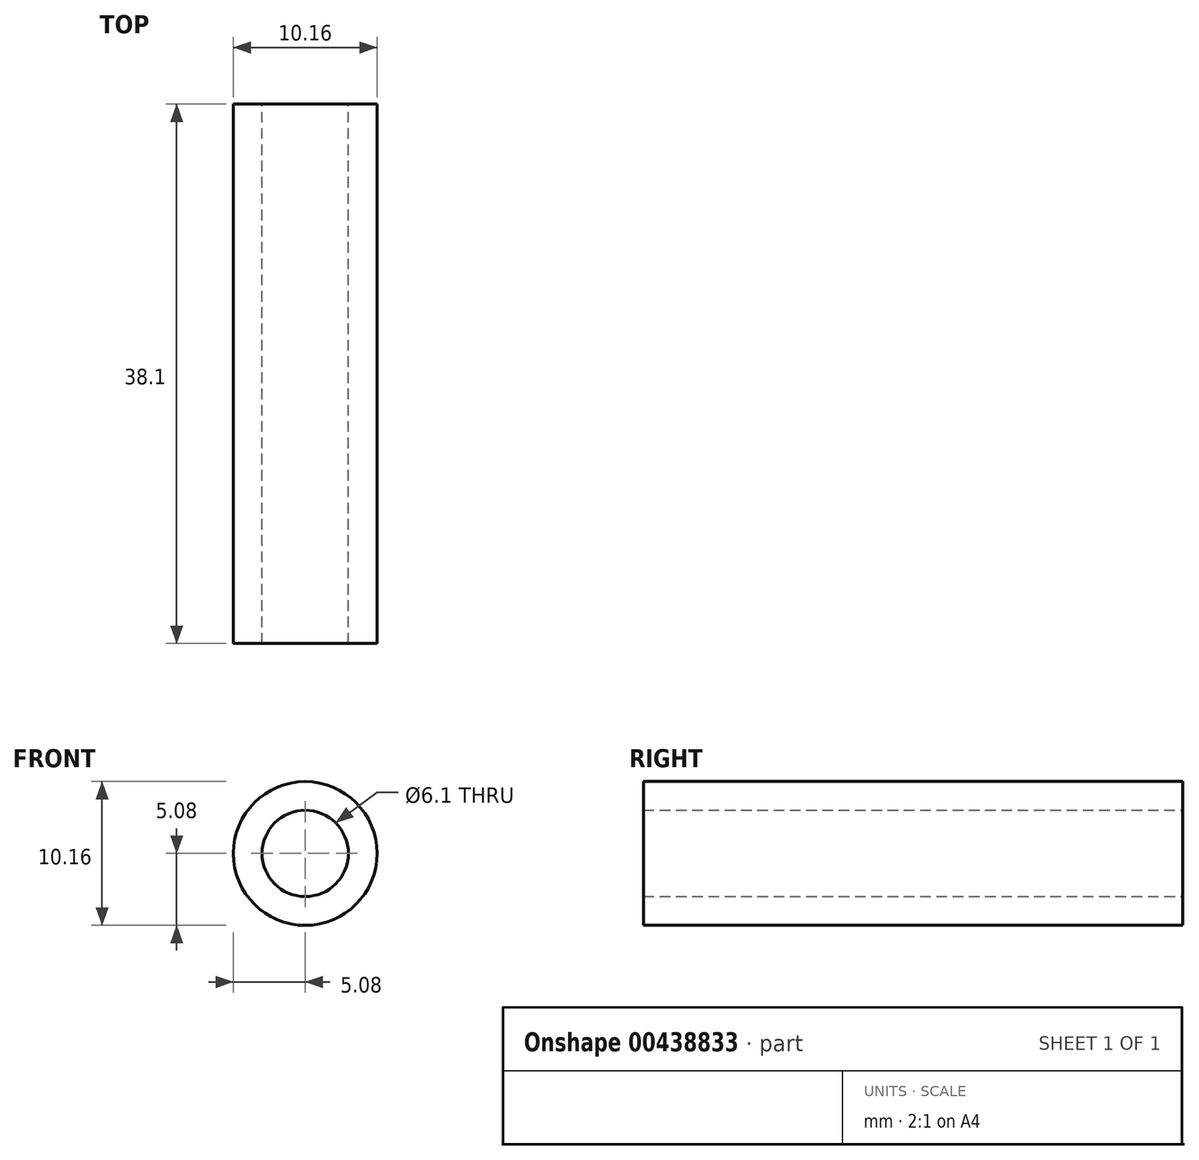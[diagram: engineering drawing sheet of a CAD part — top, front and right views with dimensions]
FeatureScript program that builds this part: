
annotation { "Feature Type Name" : "Feature", "Feature Type Description" : "" }
export const myFeature = defineFeature(function(context is Context, id is Id, definition is map)
    precondition{}
    {
        {
            var Q0;
            Q0=qCreatedBy(makeId("Front.planeOp"),FACE);
            var sketch = newSketch(context, id + "F0", { "sketchPlane" : qUnion([Q0])});
            skCircle(sketch, "E0", {"center": v(0, 0) * mm, "radius": 3.05 * mm});
            skCircle(sketch, "E1", {"center": v(0, 0) * mm, "radius": 5.08 * mm});
            skSolve(sketch);
        }
        {
            var Q0;
            Q0=makeQuery(id+"F0.imprint","IMPRINT",FACE,{"disambiguationData":[TD([[makeQuery(id+"F0.imprint","IMPRINT",EDGE,{"derivedFrom":sQuery(id+"F0.wireOp",EDGE,"E0")}),-1.0]])]});
            extrude(context, id + "F1", {"entities" : qUnion([Q0]), "depth" : 38.1 * mm, "offsetDistance" : 25.4 * mm});
        }
    });
